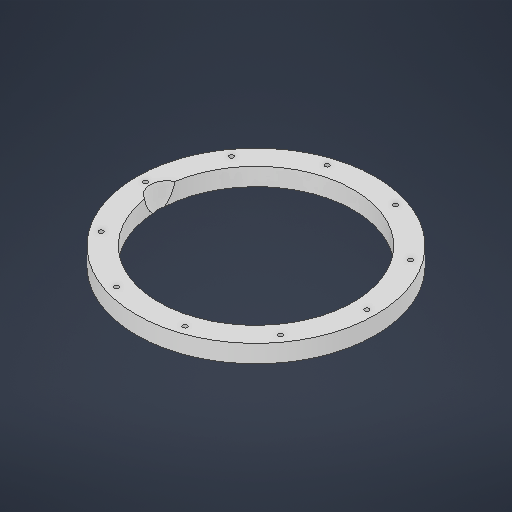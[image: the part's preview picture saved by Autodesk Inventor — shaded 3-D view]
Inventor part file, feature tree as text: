
AUTODESK INVENTOR PART (.ipt)
format: ipt  version: 2025 (Build 290162000, 162)  size: 227,328 bytes
history: native  units: in
note: dims shown in document units (in); Inventor stores cm internally (conversion verified against a paired STEP export)
features: sketch x4, extrude x2, plane x2, hole x1
ambient origin geometry x8: Origin, YZ Plane, XZ Plane, XY Plane, X Axis, Y Axis, Z Axis, Center Point
bodies: Solid1 (feature_tree)
feature tree (9):
  extrude  "Extrusion1"  Depth=8.6614in
  hole  "Hole1"  [1 undecoded]
  plane  "Work Plane6"
  plane  "Work Plane7"
  extrude  "Extrusion4"  Depth=3.937in TaperAngle=360.0deg
  sketch  "Sketch1"  dims[d0=10.6299in d1=8.6614in]
  sketch  "Sketch3"  dims[d8=0.1969in d9=3.937in d11=360.0deg]
  sketch  "Sketch Circular Pattern1"  dims[d2=0.7874in d3=0.0in d7=9.8425in]
  sketch  "Sketch5"  dims[d13=0.1969in d14=0.2362in d15=0.1575in d16=0.0787in d17=90.0deg d18=0.315in d19=0.8108in d25=2.5in d26=1.5748in d27=3.3802in d28=9.8937in d29=0.0in]
note: 1 required parameter value undecoded (feature->parameter linkage not recoverable at this tier; creation-order binding heuristic only, values carry confidence <= 0.55)
